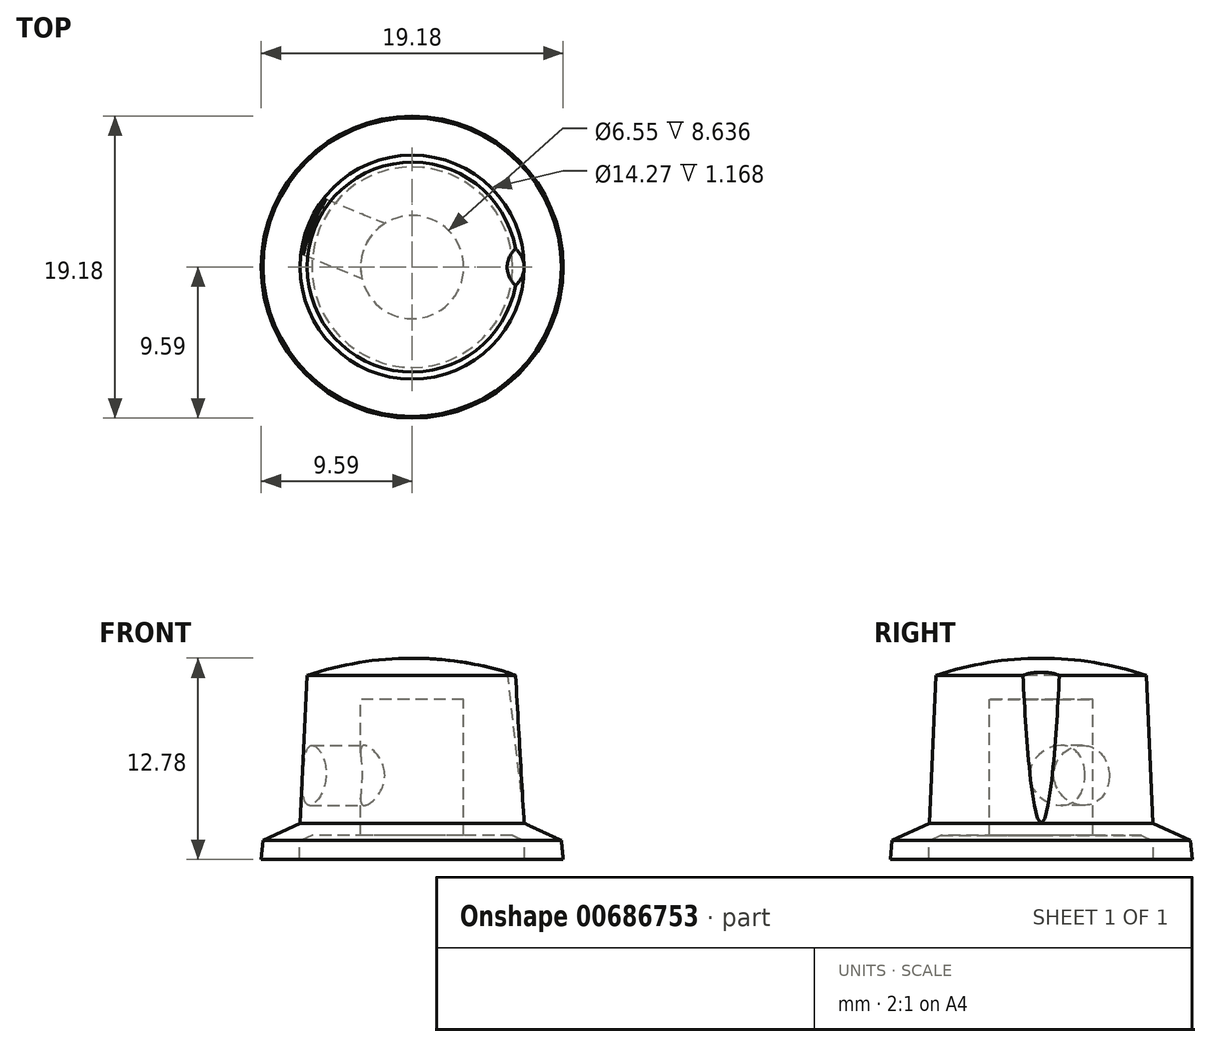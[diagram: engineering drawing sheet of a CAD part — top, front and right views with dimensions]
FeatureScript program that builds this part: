
annotation { "Feature Type Name" : "Feature", "Feature Type Description" : "" }
export const myFeature = defineFeature(function(context is Context, id is Id, definition is map)
    precondition{}
    {
        {
            var Q0;
            Q0=qCreatedBy(makeId("Front.planeOp"),FACE);
            var sketch = newSketch(context, id + "F0", { "sketchPlane" : qUnion([Q0])});
            skLineSegment(sketch, "E0", {"start": v(0, 12.78) * mm, "end": v(0, 0) * mm, "construction": true});
            skLineSegment(sketch, "E1", {"start": v(0, 10.16) * mm, "end": v(3.28, 10.16) * mm});
            skLineSegment(sketch, "E2", {"start": v(3.28, 10.16) * mm, "end": v(3.28, 1.52) * mm});
            skLineSegment(sketch, "E3", {"start": v(3.28, 1.52) * mm, "end": v(6.37, 1.52) * mm});
            skLineSegment(sketch, "E4", {"start": v(7.14, 0) * mm, "end": v(9.59, 0) * mm});
            skLineSegment(sketch, "E5", {"start": v(9.59, 0) * mm, "end": v(9.48, 1.2) * mm});
            skLineSegment(sketch, "E6", {"start": v(9.48, 1.2) * mm, "end": v(7.11, 2.29) * mm});
            skLineSegment(sketch, "E7", {"start": v(7.11, 2.29) * mm, "end": v(6.67, 11.68) * mm});
            skLineSegment(sketch, "E8", {"start": v(6.37, 1.52) * mm, "end": v(7.14, 1.17) * mm});
            skLineSegment(sketch, "E9", {"start": v(7.14, 0) * mm, "end": v(7.14, 1.17) * mm});
            skLineSegment(sketch, "E10", {"start": v(0, 12.78) * mm, "end": v(12.42, 12.78) * mm, "construction": true});
            skArc(sketch, "E11", {"start": v(6.67, 11.68) * mm, "mid": v(3.38, 12.5) * mm, "end": v(0, 12.78) * mm});
            skLineSegment(sketch, "E12", {"start": v(0, 12.78) * mm, "end": v(0, 10.16) * mm});
            skLineSegment(sketch, "E13", {"start": v(6.03, 13.37) * mm, "end": v(6.03, -0.44) * mm, "construction": true});
            skPoint(sketch, "E14", {"position": v(6.03, 11.89) * mm});
            skSolve(sketch);
        }
        {
            var Q0;
            Q0=makeQuery(id+"F0.imprint","IMPRINT",FACE,{"disambiguationData":[TD([[makeQuery(id+"F0.imprint","IMPRINT",EDGE,{"derivedFrom":sQuery(id+"F0.wireOp",EDGE,"E1")}),1.0]])]});
            var Q1;
            Q1=sQuery(id+"F0.wireOp",EDGE,"E0");
            revolve(context, id + "F1", {"entities" : qUnion([Q0]), "axis" : qUnion([Q1]), "revolveType" : RevolveType.FULL});
        }
        {
            var Q0;
            Q0=qCreatedBy(makeId("Front.planeOp"),FACE);
            var sketch = newSketch(context, id + "F2", { "sketchPlane" : qUnion([Q0])});
            skLineSegment(sketch, "E15.bottom", {"start": v(5.6, 15.8) * mm, "end": v(7.17, 15.98) * mm});
            skLineSegment(sketch, "E15.top", {"start": v(7.11, 2.29) * mm, "end": v(8.69, 2.46) * mm});
            skLineSegment(sketch, "E15.left", {"start": v(5.6, 15.8) * mm, "end": v(7.11, 2.29) * mm});
            skLineSegment(sketch, "E15.right", {"start": v(7.17, 15.98) * mm, "end": v(8.69, 2.46) * mm});
            skSolve(sketch);
        }
        {
            var Q0;
            Q0=makeQuery(id+"F2.imprint","IMPRINT",FACE,{"disambiguationData":[TD([[makeQuery(id+"F2.imprint","IMPRINT",EDGE,{"derivedFrom":sQuery(id+"F2.wireOp",EDGE,"E15.bottom")}),-1.0]])]});
            var Q1;
            Q1=sQuery(id+"F2.wireOp",EDGE,"E15.right");
            revolve(context, id + "F3", {"operationType" : NewBodyOperationType.REMOVE, "entities" : qUnion([Q0]), "axis" : qUnion([Q1]), "revolveType" : RevolveType.FULL, "oppositeDirection" : true});
        }
        {
            var Q0;
            Q0=qCreatedBy(makeId("Top.planeOp"),FACE);
            var sketch = newSketch(context, id + "F4", { "sketchPlane" : qUnion([Q0])});
            skLineSegment(sketch, "E16", {"start": v(0, 0) * mm, "end": v(9.6, 0) * mm, "construction": true});
            skLineSegment(sketch, "E17", {"start": v(9.6, 0) * mm, "end": v(0, 0) * mm, "construction": true});
            skLineSegment(sketch, "E18", {"start": v(8.86, -3.67) * mm, "end": v(0, 0) * mm, "construction": true});
            skLineSegment(sketch, "E19", {"start": v(6.6, -2.73) * mm, "end": v(8.86, -3.67) * mm});
            skSolve(sketch);
        }
        {
            var Q0;
            Q0=sQuery(id+"F4.wireOp",EDGE,"E19");
            extrude(context, id + "F5", {"bodyType" : ExtendedToolBodyType.SURFACE, "surfaceEntities" : qUnion([Q0]), "endBound" : BoundingType.UP_TO_NEXT, "depth" : 25.4 * mm, "offsetDistance" : 25.4 * mm});
        }
        {
            var Q0;
            Q0=makeQuery(id+"F5.opExtrude","SWEPT_FACE",FACE,{"disambiguationData":[OSD([sQuery(id+"F4.wireOp",EDGE,"E19")])]});
            var sketch = newSketch(context, id + "F6", { "sketchPlane" : qUnion([Q0])});
            skLineSegment(sketch, "E20.bottom", {"start": v(-12.1, 7.24) * mm, "end": v(0, 7.24) * mm});
            skLineSegment(sketch, "E20.top", {"start": v(-12.1, 5.33) * mm, "end": v(0, 5.33) * mm});
            skLineSegment(sketch, "E20.left", {"start": v(-12.1, 7.24) * mm, "end": v(-12.1, 5.33) * mm});
            skLineSegment(sketch, "E20.right", {"start": v(0, 7.24) * mm, "end": v(0, 5.33) * mm});
            skSolve(sketch);
        }
        {
            var Q0;
            Q0=makeQuery(id+"F6.imprint","IMPRINT",FACE,{"disambiguationData":[TD([[makeQuery(id+"F6.imprint","IMPRINT",EDGE,{"derivedFrom":sQuery(id+"F6.wireOp",EDGE,"E20.bottom")}),-1.0]])]});
            var Q1;
            Q1=sQuery(id+"F6.wireOp",EDGE,"E20.top");
            revolve(context, id + "F7", {"operationType" : NewBodyOperationType.REMOVE, "entities" : qUnion([Q0]), "axis" : qUnion([Q1]), "revolveType" : RevolveType.FULL, "oppositeDirection" : true});
        }
    });
